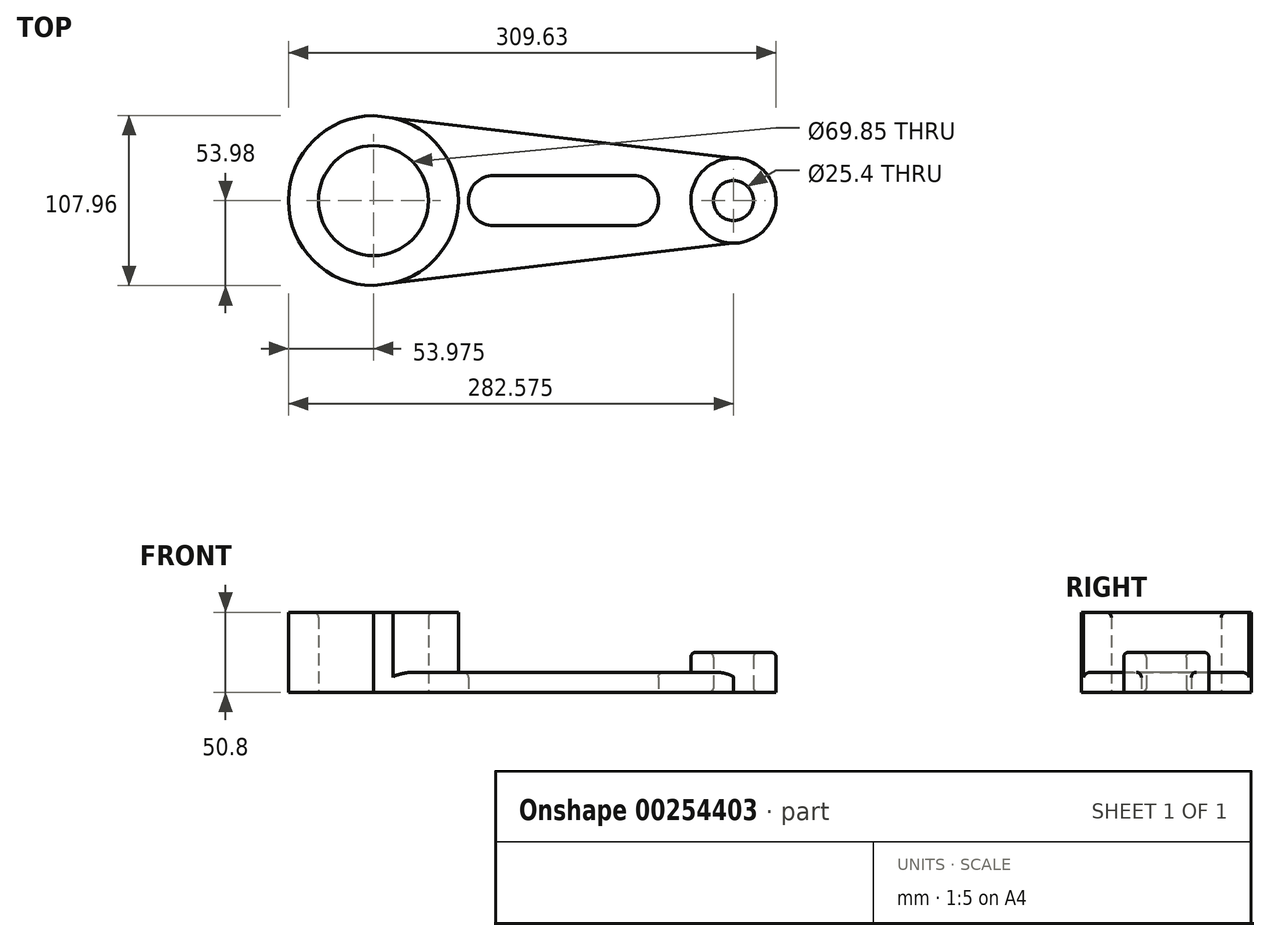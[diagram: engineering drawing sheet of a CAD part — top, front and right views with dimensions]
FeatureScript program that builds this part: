
annotation { "Feature Type Name" : "Feature", "Feature Type Description" : "" }
export const myFeature = defineFeature(function(context is Context, id is Id, definition is map)
    precondition{}
    {
        {
            var Q0;
            Q0=qCreatedBy(makeId("Top.planeOp"),FACE);
            var sketch = newSketch(context, id + "F0", { "sketchPlane" : qUnion([Q0])});
            skCircle(sketch, "E0", {"center": v(-144.45, 0) * mm, "radius": 34.93 * mm});
            skCircle(sketch, "E1", {"center": v(-144.45, 0) * mm, "radius": 53.98 * mm});
            skArc(sketch, "E2", {"start": v(-68.25, 15.88) * mm, "mid": v(-84.12, 0) * mm, "end": v(-68.25, -15.88) * mm});
            skArc(sketch, "E3", {"start": v(20.65, -15.88) * mm, "mid": v(36.53, 0) * mm, "end": v(20.65, 15.88) * mm});
            skCircle(sketch, "E4", {"center": v(84.15, 0) * mm, "radius": 12.7 * mm});
            skCircle(sketch, "E5", {"center": v(84.15, 0) * mm, "radius": 27.05 * mm});
            skLineSegment(sketch, "E6", {"start": v(-68.25, 15.87) * mm, "end": v(20.65, 15.87) * mm});
            skLineSegment(sketch, "E7", {"start": v(-68.25, -15.87) * mm, "end": v(20.65, -15.87) * mm});
            skLineSegment(sketch, "E8", {"start": v(84.15, 0) * mm, "end": v(84.15, 27.05) * mm});
            skLineSegment(sketch, "E9", {"start": v(84.15, 27.05) * mm, "end": v(84.15, -27.05) * mm});
            skLineSegment(sketch, "E10", {"start": v(-144.45, 53.98) * mm, "end": v(84.15, 27.05) * mm});
            skLineSegment(sketch, "E11", {"start": v(-144.45, -53.98) * mm, "end": v(84.15, -27.05) * mm});
            skSolve(sketch);
        }
        {
            var Q0;
            Q0=makeQuery(id+"F0.imprint","IMPRINT",FACE,{"disambiguationData":[TD([[makeQuery(id+"F0.imprint","IMPRINT",EDGE,{"derivedFrom":sQuery(id+"F0.wireOp",EDGE,"E0")}),-1.0]])]});
            extrude(context, id + "F1", {"entities" : qUnion([Q0]), "depth" : 50.8 * mm});
        }
        {
            var Q0;
            Q0=makeQuery(id+"F0.imprint","IMPRINT",FACE,{"disambiguationData":[TD([[makeQuery(id+"F0.imprint","IMPRINT",EDGE,{"derivedFrom":sQuery(id+"F0.wireOp",EDGE,"E2")}),-1.0]])]});
            extrude(context, id + "F2", {"entities" : qUnion([Q0]), "operationType" : NewBodyOperationType.ADD, "depth" : 12.7 * mm});
        }
        {
            var Q0;
            {var subQ0=sQuery(id+"F0.wireOp",EDGE,"E9");var subQ1=sQuery(id+"F0.wireOp",EDGE,"E4");var subQ2=makeQuery(id+"F0.imprint","INTERSECT",VERTEX,{"disambiguationData":[OD(0.0)],"derivedFrom":[subQ1,subQ0]});Q0=makeQuery(id+"F0.imprint","IMPRINT",FACE,{"disambiguationData":[TD([[makeQuery(id+"F0.imprint","IMPRINT",EDGE,{"disambiguationData":[TD([[subQ2,1.0]])],"derivedFrom":subQ1}),-1.0]])]});}
            var Q1;
            {var subQ0=sQuery(id+"F0.wireOp",EDGE,"E9");var subQ1=sQuery(id+"F0.wireOp",EDGE,"E4");var subQ2=makeQuery(id+"F0.imprint","INTERSECT",VERTEX,{"disambiguationData":[OD(0.0)],"derivedFrom":[subQ1,subQ0]});Q1=makeQuery(id+"F0.imprint","IMPRINT",FACE,{"disambiguationData":[TD([[makeQuery(id+"F0.imprint","IMPRINT",EDGE,{"disambiguationData":[TD([[subQ2,-1.0]])],"derivedFrom":subQ1}),-1.0]])]});}
            extrude(context, id + "F3", {"entities" : qUnion([Q0, Q1]), "operationType" : NewBodyOperationType.ADD, "depth" : 25.4 * mm});
        }
        {
            var Q0;
            {var subQ0=sQuery(id+"F0.wireOp",EDGE,"E1");Q0=makeQuery(id+"F1.opExtrude","CAP_EDGE",EDGE,{"disambiguationData":[OSD([subQ0]),TDD([makeQuery(id+"F0.imprint","IMPRINT",EDGE,{"disambiguationData":[TD([[makeQuery(id+"F0.imprint","INTERSECT",VERTEX,{"disambiguationData":[OD(0.0)],"derivedFrom":[subQ0,sQuery(id+"F0.wireOp",EDGE,"E10")]}),-1.0]])],"derivedFrom":subQ0})])],"isStart":false});}
            var Q1;
            {var subQ0=sQuery(id+"F0.wireOp",EDGE,"E1");Q1=makeQuery(id+"F1.opExtrude","CAP_EDGE",EDGE,{"disambiguationData":[OSD([subQ0]),TDD([makeQuery(id+"F0.imprint","IMPRINT",EDGE,{"disambiguationData":[TD([[makeQuery(id+"F0.imprint","INTERSECT",VERTEX,{"disambiguationData":[OD(1.0)],"derivedFrom":[subQ0,sQuery(id+"F0.wireOp",EDGE,"E10")]}),1.0]])],"derivedFrom":subQ0})])],"isStart":false});}
            var Q2;
            Q2=makeQuery(id+"F2.opExtrude","CAP_EDGE",EDGE,{"disambiguationData":[OSD([sQuery(id+"F0.wireOp",EDGE,"E11")])],"isStart":false});
            var Q3;
            Q3=makeQuery(id+"F2.opExtrude","CAP_EDGE",EDGE,{"disambiguationData":[OSD([sQuery(id+"F0.wireOp",EDGE,"E10")])],"isStart":false});
            var Q4;
            Q4=makeQuery(id+"F3.opExtrude","CAP_EDGE",EDGE,{"disambiguationData":[OSD([sQuery(id+"F0.wireOp",EDGE,"E5")])],"isStart":false});
            fillet(context, id + "F4", {"entities" : qUnion([Q0, Q1, Q2, Q3, Q4]), "radius" : 3.17 * mm, "tangentPropagation" : true, "allowEdgeOverflow" : false});
        }
        {
            var Q0;
            Q0=makeQuery(id+"F1.opExtrude","CAP_EDGE",EDGE,{"disambiguationData":[OSD([sQuery(id+"F0.wireOp",EDGE,"E0")])],"isStart":false});
            var Q1;
            Q1=makeQuery(id+"F2.opExtrude","CAP_EDGE",EDGE,{"disambiguationData":[OSD([sQuery(id+"F0.wireOp",EDGE,"E7")])],"isStart":false});
            var Q2;
            Q2=makeQuery(id+"F3.opExtrude","SWEPT_FACE",FACE,{"disambiguationData":[OSD([sQuery(id+"F0.wireOp",EDGE,"E4")])]});
            fillet(context, id + "F5", {"entities" : qUnion([Q0, Q1, Q2]), "radius" : 3.17 * mm, "tangentPropagation" : true, "allowEdgeOverflow" : false});
        }
    });
